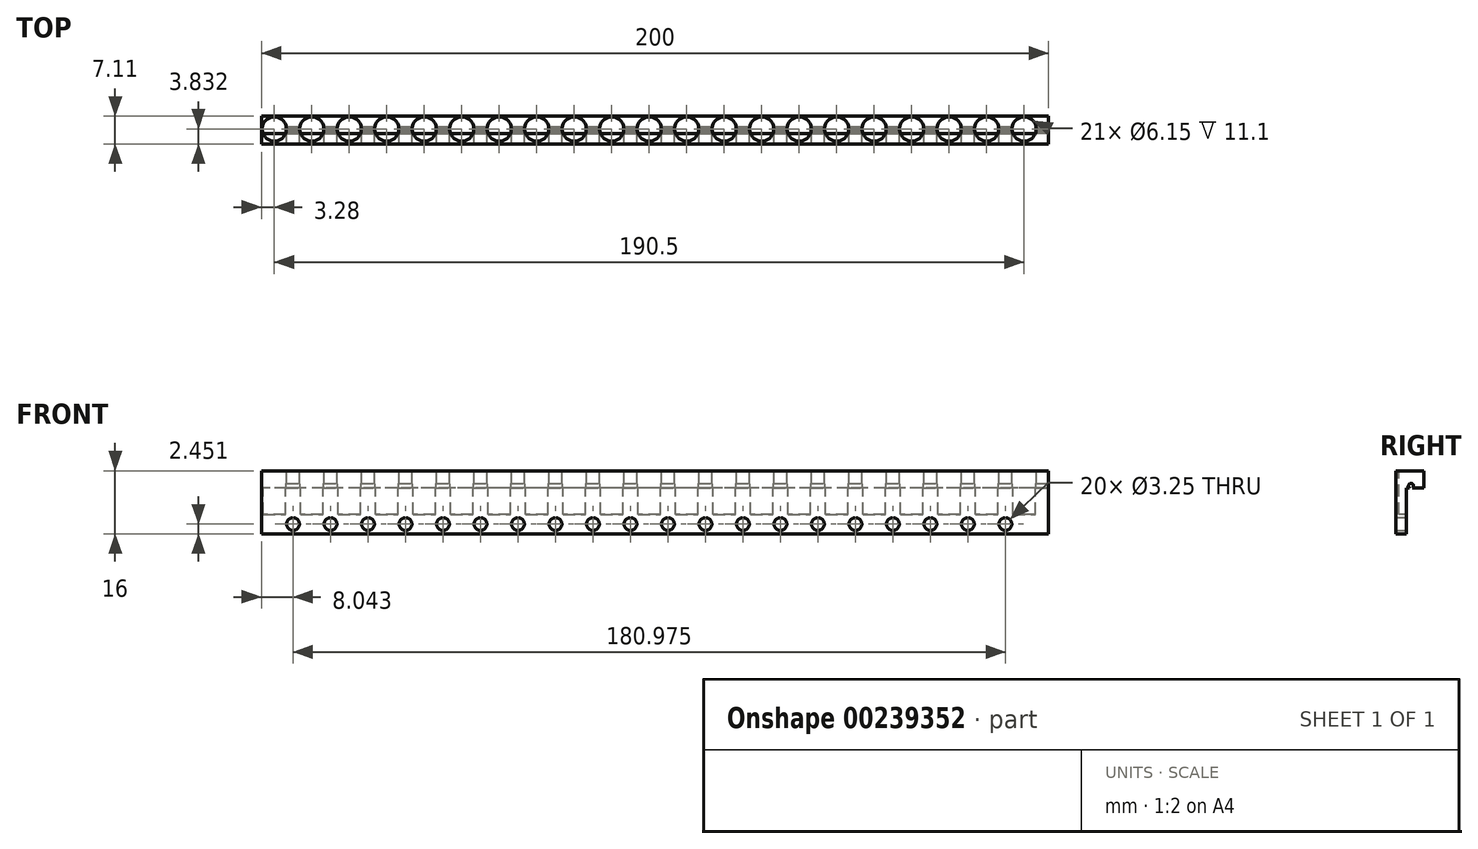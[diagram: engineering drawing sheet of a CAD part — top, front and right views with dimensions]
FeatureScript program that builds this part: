
annotation { "Feature Type Name" : "Feature", "Feature Type Description" : "" }
export const myFeature = defineFeature(function(context is Context, id is Id, definition is map)
    precondition{}
    {
        {
            var Q0;
            Q0=qCreatedBy(makeId("Right.planeOp"),FACE);
            var sketch = newSketch(context, id + "F0", { "sketchPlane" : qUnion([Q0])});
            skLineSegment(sketch, "E0.bottom", {"start": v(0, 0) * mm, "end": v(2.64, 0) * mm});
            skLineSegment(sketch, "E0.left", {"start": v(0, 0) * mm, "end": v(0, 16) * mm});
            skLineSegment(sketch, "E0.right", {"start": v(2.64, 0) * mm, "end": v(2.64, 11.68) * mm});
            skLineSegment(sketch, "E1.bottom", {"start": v(0, 16) * mm, "end": v(7.11, 16) * mm});
            skLineSegment(sketch, "E1.top", {"start": v(2.64, 11.68) * mm, "end": v(7.11, 11.68) * mm});
            skLineSegment(sketch, "E1.right", {"start": v(7.11, 16) * mm, "end": v(7.11, 11.68) * mm});
            skSolve(sketch);
        }
        {
            var Q0;
            Q0 = qSketchRegion(id + "F0", true);
            extrude(context, id + "F1", {"entities" : qUnion([Q0]), "depth" : 200 * mm});
        }
        {
            var Q0;
            Q0=makeQuery(id+"F1.opExtrude","SWEPT_FACE",FACE,{"disambiguationData":[OSD([sQuery(id+"F0.wireOp",EDGE,"E1.bottom")])]});
            var sketch = newSketch(context, id + "F2", { "sketchPlane" : qUnion([Q0])});
            skCircle(sketch, "E2", {"center": v(3.28, 3.83) * mm, "radius": 3.08 * mm});
            skCircle(sketch, "E3.1.0.0", {"center": v(12.8, 3.83) * mm, "radius": 3.08 * mm});
            skCircle(sketch, "E3.2.0.0", {"center": v(22.33, 3.83) * mm, "radius": 3.08 * mm});
            skCircle(sketch, "E3.3.0.0", {"center": v(31.86, 3.83) * mm, "radius": 3.08 * mm});
            skCircle(sketch, "E3.4.0.0", {"center": v(41.38, 3.83) * mm, "radius": 3.08 * mm});
            skCircle(sketch, "E3.5.0.0", {"center": v(50.9, 3.83) * mm, "radius": 3.08 * mm});
            skCircle(sketch, "E3.6.0.0", {"center": v(60.43, 3.83) * mm, "radius": 3.08 * mm});
            skCircle(sketch, "E3.7.0.0", {"center": v(69.95, 3.83) * mm, "radius": 3.08 * mm});
            skCircle(sketch, "E3.8.0.0", {"center": v(79.48, 3.83) * mm, "radius": 3.08 * mm});
            skCircle(sketch, "E3.9.0.0", {"center": v(89, 3.83) * mm, "radius": 3.08 * mm});
            skLineSegment(sketch, "E3.direction1", {"start": v(3.28, 3.83) * mm, "end": v(12.8, 3.83) * mm, "construction": true});
            skCircle(sketch, "E4.0.10.0", {"center": v(98.53, 3.83) * mm, "radius": 3.08 * mm});
            skCircle(sketch, "E4.0.11.0", {"center": v(108.06, 3.83) * mm, "radius": 3.08 * mm});
            skCircle(sketch, "E4.0.12.0", {"center": v(117.58, 3.83) * mm, "radius": 3.08 * mm});
            skCircle(sketch, "E4.0.13.0", {"center": v(127.1, 3.83) * mm, "radius": 3.08 * mm});
            skCircle(sketch, "E4.0.14.0", {"center": v(136.63, 3.83) * mm, "radius": 3.08 * mm});
            skCircle(sketch, "E4.0.15.0", {"center": v(146.16, 3.83) * mm, "radius": 3.08 * mm});
            skCircle(sketch, "E4.0.16.0", {"center": v(155.68, 3.83) * mm, "radius": 3.08 * mm});
            skCircle(sketch, "E4.0.17.0", {"center": v(165.2, 3.83) * mm, "radius": 3.08 * mm});
            skCircle(sketch, "E4.0.18.0", {"center": v(174.73, 3.83) * mm, "radius": 3.08 * mm});
            skCircle(sketch, "E4.0.19.0", {"center": v(184.25, 3.83) * mm, "radius": 3.08 * mm});
            skCircle(sketch, "E5.0.20.0", {"center": v(193.78, 3.83) * mm, "radius": 3.08 * mm});
            skSolve(sketch);
        }
        {
            var Q0;
            Q0 = qSketchRegion(id + "F2", true);
            extrude(context, id + "F3", {"entities" : qUnion([Q0]), "operationType" : NewBodyOperationType.REMOVE, "oppositeDirection" : true, "depth" : 11.1 * mm});
        }
        {
            var Q0;
            Q0=makeQuery(id+"F1.opExtrude","CAP_FACE",FACE,{"disambiguationData":[OSD([sQuery(id+"F0.wireOp",EDGE,"E0.bottom"),sQuery(id+"F0.wireOp",EDGE,"E0.left"),sQuery(id+"F0.wireOp",EDGE,"E0.right"),sQuery(id+"F0.wireOp",EDGE,"E1.bottom"),sQuery(id+"F0.wireOp",EDGE,"E1.top"),sQuery(id+"F0.wireOp",EDGE,"E1.right")])],"isStart":false});
            var sketch = newSketch(context, id + "F4", { "sketchPlane" : qUnion([Q0])});
            skCircle(sketch, "E6", {"center": v(3.83, 12.18) * mm, "radius": 0.64 * mm});
            skSolve(sketch);
        }
        {
            var Q0;
            Q0 = qSketchRegion(id + "F4", true);
            extrude(context, id + "F5", {"entities" : qUnion([Q0]), "operationType" : NewBodyOperationType.REMOVE, "endBound" : BoundingType.THROUGH_ALL, "oppositeDirection" : true, "depth" : 25 * mm});
        }
        {
            var Q0;
            Q0=makeQuery(id+"F1.opExtrude","SWEPT_FACE",FACE,{"disambiguationData":[OSD([sQuery(id+"F0.wireOp",EDGE,"E0.right")])]});
            var sketch = newSketch(context, id + "F6", { "sketchPlane" : qUnion([Q0])});
            skLineSegment(sketch, "E7", {"start": v(-190.94, 4.9) * mm, "end": v(-187.1, 4.9) * mm, "construction": true});
            skLineSegment(sketch, "E8", {"start": v(-189.02, 4.9) * mm, "end": v(-189.02, 0) * mm, "construction": true});
            skLineSegment(sketch, "E9", {"start": v(-189.02, 2.45) * mm, "end": v(-195.84, 2.45) * mm, "construction": true});
            skCircle(sketch, "E10", {"center": v(-189.02, 2.45) * mm, "radius": 1.63 * mm});
            skCircle(sketch, "E11.1.0.0", {"center": v(-179.5, 2.45) * mm, "radius": 1.63 * mm});
            skCircle(sketch, "E11.2.0.0", {"center": v(-169.97, 2.45) * mm, "radius": 1.63 * mm});
            skCircle(sketch, "E11.3.0.0", {"center": v(-160.44, 2.45) * mm, "radius": 1.63 * mm});
            skCircle(sketch, "E11.4.0.0", {"center": v(-150.92, 2.45) * mm, "radius": 1.63 * mm});
            skCircle(sketch, "E11.5.0.0", {"center": v(-141.4, 2.45) * mm, "radius": 1.63 * mm});
            skCircle(sketch, "E11.6.0.0", {"center": v(-131.87, 2.45) * mm, "radius": 1.63 * mm});
            skCircle(sketch, "E11.7.0.0", {"center": v(-122.34, 2.45) * mm, "radius": 1.63 * mm});
            skCircle(sketch, "E11.8.0.0", {"center": v(-112.82, 2.45) * mm, "radius": 1.63 * mm});
            skCircle(sketch, "E11.9.0.0", {"center": v(-103.3, 2.45) * mm, "radius": 1.63 * mm});
            skCircle(sketch, "E11.10.0.0", {"center": v(-93.77, 2.45) * mm, "radius": 1.63 * mm});
            skCircle(sketch, "E11.11.0.0", {"center": v(-84.24, 2.45) * mm, "radius": 1.63 * mm});
            skCircle(sketch, "E11.12.0.0", {"center": v(-74.72, 2.45) * mm, "radius": 1.63 * mm});
            skCircle(sketch, "E11.13.0.0", {"center": v(-65.2, 2.45) * mm, "radius": 1.63 * mm});
            skCircle(sketch, "E11.14.0.0", {"center": v(-55.67, 2.45) * mm, "radius": 1.63 * mm});
            skCircle(sketch, "E11.15.0.0", {"center": v(-46.14, 2.45) * mm, "radius": 1.63 * mm});
            skCircle(sketch, "E11.16.0.0", {"center": v(-36.62, 2.45) * mm, "radius": 1.63 * mm});
            skCircle(sketch, "E11.17.0.0", {"center": v(-27.1, 2.45) * mm, "radius": 1.63 * mm});
            skCircle(sketch, "E11.18.0.0", {"center": v(-17.57, 2.45) * mm, "radius": 1.63 * mm});
            skCircle(sketch, "E11.19.0.0", {"center": v(-8.04, 2.45) * mm, "radius": 1.63 * mm});
            skLineSegment(sketch, "E11.direction1", {"start": v(-189.02, 2.45) * mm, "end": v(-179.5, 2.45) * mm, "construction": true});
            skSolve(sketch);
        }
        {
            var Q0;
            Q0 = qSketchRegion(id + "F6", true);
            extrude(context, id + "F7", {"entities" : qUnion([Q0]), "operationType" : NewBodyOperationType.REMOVE, "endBound" : BoundingType.THROUGH_ALL, "oppositeDirection" : true, "depth" : 25 * mm});
        }
    });
